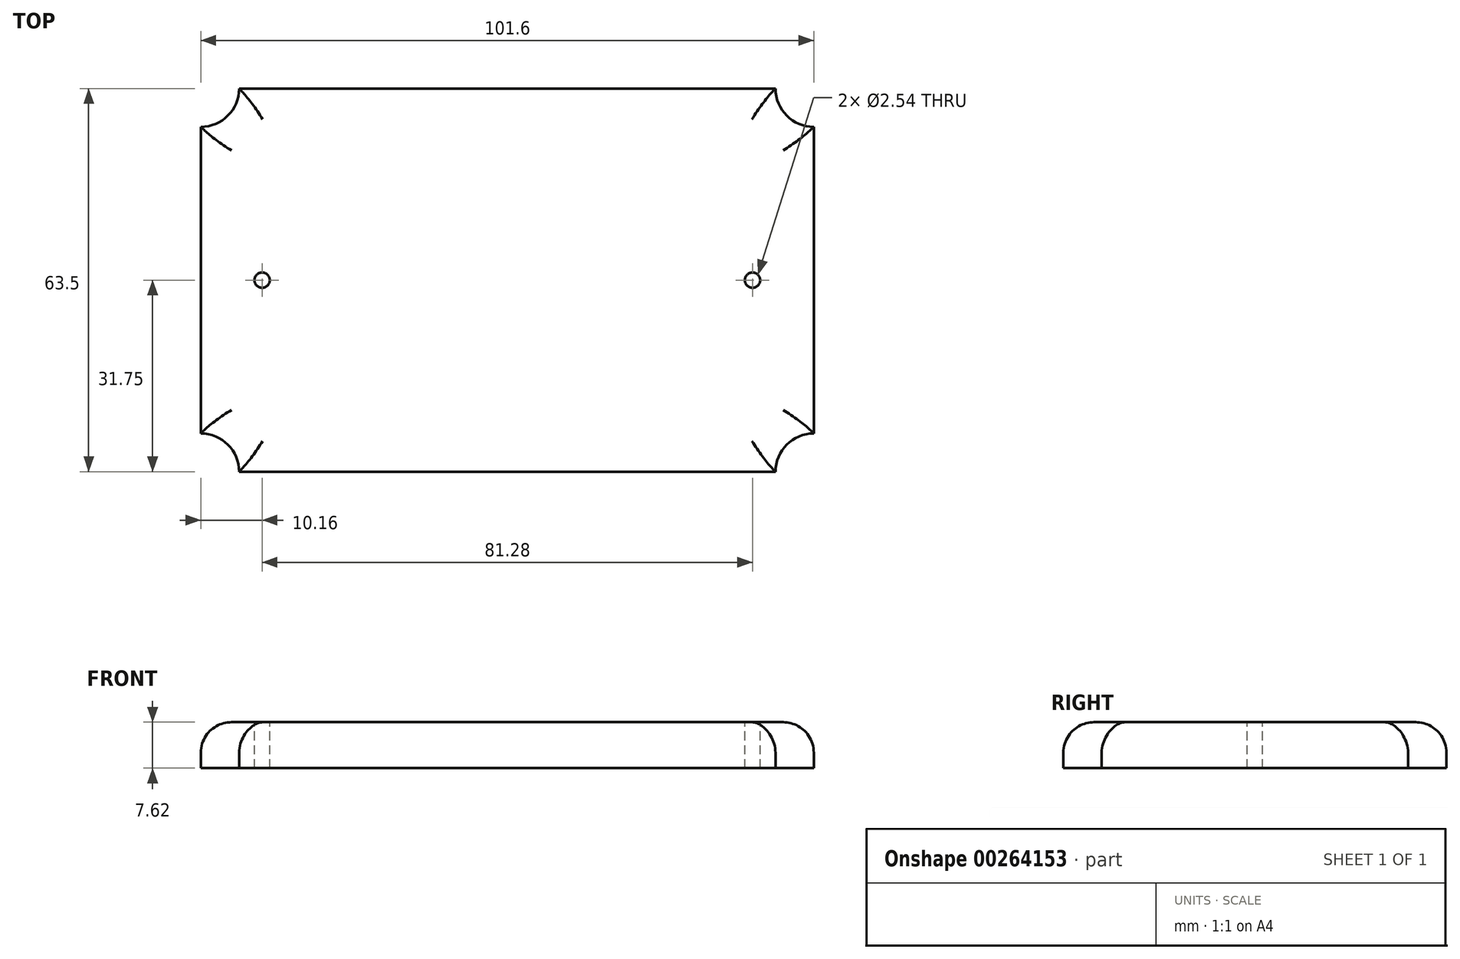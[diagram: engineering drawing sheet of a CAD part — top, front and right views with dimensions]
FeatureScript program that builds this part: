
annotation { "Feature Type Name" : "Feature", "Feature Type Description" : "" }
export const myFeature = defineFeature(function(context is Context, id is Id, definition is map)
    precondition{}
    {
        {
            var Q0;
            Q0=qCreatedBy(makeId("Top.planeOp"),FACE);
            var sketch = newSketch(context, id + "F0", { "sketchPlane" : qUnion([Q0])});
            skLineSegment(sketch, "E0.bottom", {"start": v(-50.8, 31.75) * mm, "end": v(50.8, 31.75) * mm});
            skLineSegment(sketch, "E0.top", {"start": v(-50.8, -31.75) * mm, "end": v(50.8, -31.75) * mm});
            skLineSegment(sketch, "E0.left", {"start": v(-50.8, 31.75) * mm, "end": v(-50.8, -31.75) * mm});
            skLineSegment(sketch, "E0.right", {"start": v(50.8, 31.75) * mm, "end": v(50.8, -31.75) * mm});
            skPoint(sketch, "E0.middle", {"position": v(0, 0) * mm});
            skCircle(sketch, "E1", {"center": v(-50.8, 31.75) * mm, "radius": 6.35 * mm});
            skCircle(sketch, "E2.MirrorC", {"center": v(50.8, 31.75) * mm, "radius": 6.35 * mm});
            skCircle(sketch, "E3.MirrorC", {"center": v(-50.8, -31.75) * mm, "radius": 6.35 * mm});
            skCircle(sketch, "E4.MirrorC", {"center": v(50.8, -31.75) * mm, "radius": 6.35 * mm});
            skSolve(sketch);
        }
        {
            var Q0;
            {var subQ5=sQuery(id+"F0.wireOp",EDGE,"E1");var subQ13=sQuery(id+"F0.wireOp",EDGE,"E0.bottom");var subQ14=makeQuery(id+"F0.imprint","INTERSECT",VERTEX,{"derivedFrom":[subQ13,subQ5]});Q0=makeQuery(id+"F0.imprint","IMPRINT",FACE,{"disambiguationData":[TD([[makeQuery(id+"F0.imprint","IMPRINT",EDGE,{"disambiguationData":[TD([[subQ14,-1.0]])],"derivedFrom":subQ13}),-1.0]])]});}
            extrude(context, id + "F1", {"entities" : qUnion([Q0]), "depth" : 7.62 * mm});
        }
        {
            var Q0;
            Q0=makeQuery(id+"F1.opExtrude","CAP_EDGE",EDGE,{"disambiguationData":[OSD([sQuery(id+"F0.wireOp",EDGE,"E0.bottom")])],"isStart":false});
            var Q1;
            Q1=makeQuery(id+"F1.opExtrude","CAP_EDGE",EDGE,{"disambiguationData":[OSD([sQuery(id+"F0.wireOp",EDGE,"E0.left")])],"isStart":false});
            var Q2;
            Q2=makeQuery(id+"F1.opExtrude","CAP_EDGE",EDGE,{"disambiguationData":[OSD([sQuery(id+"F0.wireOp",EDGE,"E0.right")])],"isStart":false});
            var Q3;
            Q3=makeQuery(id+"F1.opExtrude","CAP_EDGE",EDGE,{"disambiguationData":[OSD([sQuery(id+"F0.wireOp",EDGE,"E0.top")])],"isStart":false});
            var Q4;
            Q4=makeQuery(id+"F1.opExtrude","CAP_EDGE",EDGE,{"disambiguationData":[OSD([sQuery(id+"F0.wireOp",EDGE,"E1")])],"isStart":false});
            var Q5;
            Q5=makeQuery(id+"F1.opExtrude","CAP_EDGE",EDGE,{"disambiguationData":[OSD([sQuery(id+"F0.wireOp",EDGE,"E3.MirrorC")])],"isStart":false});
            var Q6;
            Q6=makeQuery(id+"F1.opExtrude","CAP_EDGE",EDGE,{"disambiguationData":[OSD([sQuery(id+"F0.wireOp",EDGE,"E4.MirrorC")])],"isStart":false});
            var Q7;
            Q7=makeQuery(id+"F1.opExtrude","CAP_EDGE",EDGE,{"disambiguationData":[OSD([sQuery(id+"F0.wireOp",EDGE,"E2.MirrorC")])],"isStart":false});
            fillet(context, id + "F2", {"entities" : qUnion([Q0, Q1, Q2, Q3, Q4, Q5, Q6, Q7]), "radius" : 5.08 * mm, "tangentPropagation" : true, "allowEdgeOverflow" : false});
        }
        {
            var Q0;
            Q0=makeQuery(id+"F1.opExtrude","CAP_FACE",FACE,{"disambiguationData":[OSD([sQuery(id+"F0.wireOp",EDGE,"E0.bottom"),sQuery(id+"F0.wireOp",EDGE,"E0.top"),sQuery(id+"F0.wireOp",EDGE,"E0.left"),sQuery(id+"F0.wireOp",EDGE,"E0.right"),sQuery(id+"F0.wireOp",EDGE,"E1"),sQuery(id+"F0.wireOp",EDGE,"E2.MirrorC"),sQuery(id+"F0.wireOp",EDGE,"E3.MirrorC"),sQuery(id+"F0.wireOp",EDGE,"E4.MirrorC")])],"isStart":false});
            var sketch = newSketch(context, id + "F3", { "sketchPlane" : qUnion([Q0])});
            skCircle(sketch, "E5", {"center": v(-40.64, 0) * mm, "radius": 1.27 * mm});
            skCircle(sketch, "E6", {"center": v(40.64, 0) * mm, "radius": 1.27 * mm});
            skSolve(sketch);
        }
        {
            var Q0;
            Q0=makeQuery(id+"F3.imprint","IMPRINT",FACE,{"disambiguationData":[TD([[makeQuery(id+"F3.imprint","IMPRINT",EDGE,{"derivedFrom":sQuery(id+"F3.wireOp",EDGE,"E5")}),1.0]])]});
            var Q1;
            Q1=makeQuery(id+"F3.imprint","IMPRINT",FACE,{"disambiguationData":[TD([[makeQuery(id+"F3.imprint","IMPRINT",EDGE,{"derivedFrom":sQuery(id+"F3.wireOp",EDGE,"E6")}),1.0]])]});
            extrude(context, id + "F4", {"entities" : qUnion([Q0, Q1]), "operationType" : NewBodyOperationType.REMOVE, "oppositeDirection" : true, "depth" : 25.4 * mm});
        }
    });
